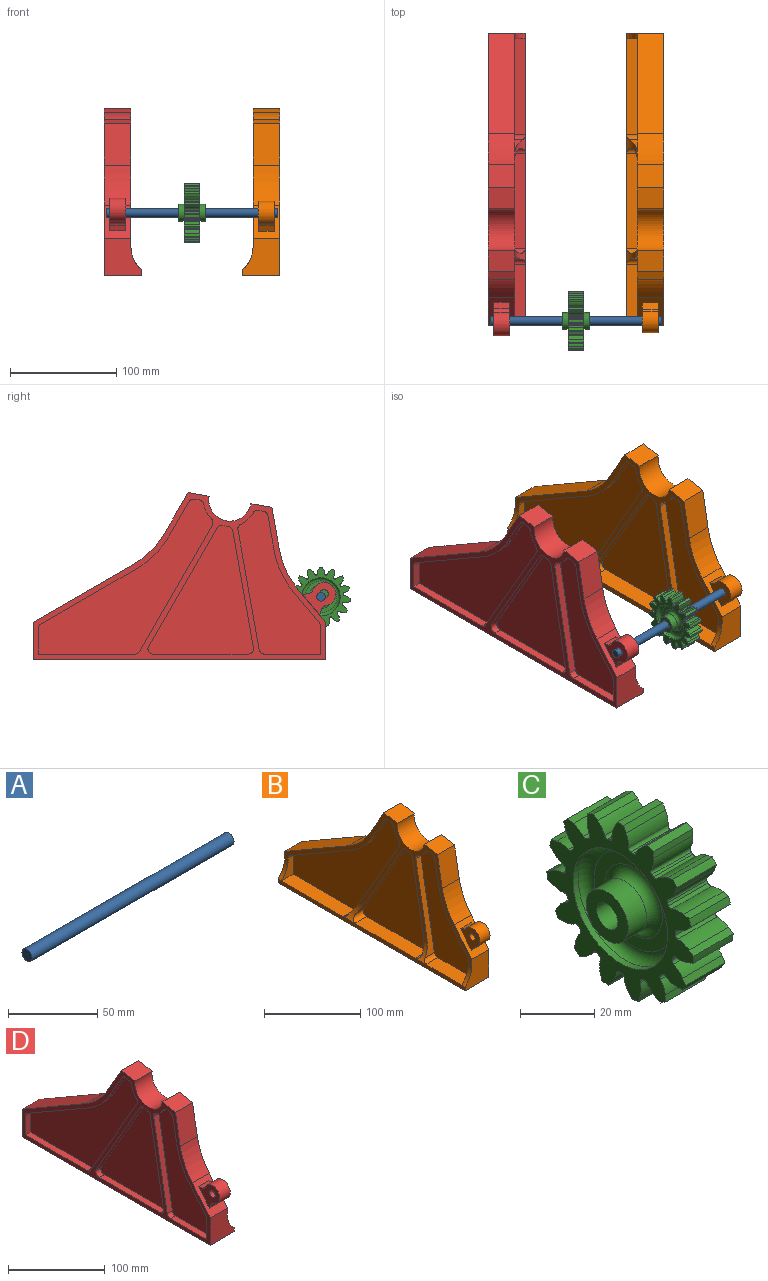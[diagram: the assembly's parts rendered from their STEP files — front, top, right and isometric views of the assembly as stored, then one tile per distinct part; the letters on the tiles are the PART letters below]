
ASSEMBLY  parts=4 mates=3
PART A: 3 faces, bbox 160x8x8 mm
  f0: cylinder r=4mm len=160mm, axis (-1,0,0), area 4021.2mm2, adj f1,f2
  f1: plane 8x8mm, normal (1,0,0), area 50.3mm2, adj f0
  f2: plane 8x8mm, normal (-1,0,0), area 50.3mm2, adj f0
PART B: 100 faces, bbox 35x281.6x156.9 mm
  f0: plane 31.19x26.17mm, normal (0,-0.77,0.64), area 642.9mm2, adj f29,f30,f36,f43,f92,f94,f96,f97
  f1: plane 89.24x17.5mm, normal (0,0,1), area 1561.7mm2, adj f7,f41,f64,f69
  f2: plane 90.51x17.5mm, normal (0,0,1), area 1583.9mm2, adj f15,f41,f54,f65
  f3: plane 90.51x7.5mm, normal (0,0,1), area 678.8mm2, adj f17,f22,f29,f73
  f4: cylinder r=25mm len=7.5mm, axis (1,0,0), area 36.1mm2, adj f8,f29,f71,f78
  f5: cylinder r=25mm len=7.5mm, axis (1,0,0), area 36.1mm2, adj f7,f30,f63,f70
  f6: plane 52.7x17.5mm, normal (0,0,1), area 922.2mm2, adj f14,f41,f53,f68
  f7: plane 121.09x99.24mm, normal (-1,0,0), area 7013.7mm2, adj f1,f5,f58,f61,f63,f64,f69,f70
  f8: plane 121.09x99.24mm, normal (1,0,0), area 7013.7mm2, adj f4,f9,f55,f60,f71,f72,f77,f78
  f9: plane 89.24x7.5mm, normal (0,0,1), area 669.3mm2, adj f8,f29,f72,f77
  f10: cylinder r=25mm len=11.41mm, axis (1,0,0), area 118mm2, adj f16,f29,f75,f81
  f11: cylinder r=25mm len=13.72mm, axis (1,0,0), area 118mm2, adj f17,f29,f74,f82
  f12: cylinder r=25mm len=11.41mm, axis (1,0,0), area 118mm2, adj f14,f30,f67,f88
  f13: cylinder r=25mm len=13.72mm, axis (1,0,0), area 118mm2, adj f15,f30,f66,f87
  f14: plane 135.24x77.57mm, normal (-1,0,0), area 5541.1mm2, adj f6,f12,f23,f27,f28,f50,f53,f57
  f15: plane 163.98x145.88mm, normal (-1,0,0), area 9003.2mm2, adj f2,f13,f24,f25,f26,f49,f54,f62
  f16: plane 135.24x77.57mm, normal (1,0,0), area 5541.1mm2, adj f10,f19,f20,f21,f45,f51,f52,f56
  f17: plane 163.98x146.41mm, normal (1,0,0), area 9005.4mm2, adj f3,f11,f18,f22,f46,f47,f48,f59
  f18: plane 8.09x7.5mm, normal (0,0.17,-0.98), area 61.6mm2, adj f17,f29,f48,f82
  f19: plane 7.5x4.64mm, normal (0,0.17,-0.98), area 35.4mm2, adj f16,f29,f81,f83
  f20: plane 26.36x7.5mm, normal (0,1,0), area 197.7mm2, adj f16,f21,f29,f79
  f21: plane 52.7x7.5mm, normal (0,0,1), area 395.2mm2, adj f16,f20,f29,f76
  f22: plane 24.23x7.5mm, normal (0,-1,0), area 181.7mm2, adj f3,f17,f29,f80
  f23: plane 28.4x23.83mm, normal (0,0.77,-0.64), area 278.1mm2, adj f14,f28,f30,f84
  f24: plane 89.24x51.52mm, normal (0,-0.5,-0.87), area 772.8mm2, adj f15,f25,f30,f85
  f25: cylinder r=85mm len=31.11mm, axis (1,0,0), area 333.8mm2, adj f15,f24,f26,f30
  f26: plane 32.19x18.59mm, normal (0,-0.87,-0.5), area 278.8mm2, adj f15,f25,f30,f86
  f27: plane 32.44x7.5mm, normal (0,0.98,-0.17), area 247mm2, adj f14,f28,f30,f89
  f28: cylinder r=85mm len=39.88mm, axis (1,0,0), area 333.8mm2, adj f14,f23,f27,f30
  f29: plane 275x156.95mm, normal (1,0,0), area 5097.7mm2, adj f0,f3,f4,f9,f10,f11,f18,f19
  f30: plane 275x129.59mm, normal (-1,0,0), area 3228.7mm2, adj f0,f5,f12,f13,f23,f24,f25,f26
  f31: cylinder r=30mm len=22.36mm, axis (0,-1,0), area 126.2mm2, adj f30,f36,f41,f53
  f32: plane 25x19.7mm, normal (0,-0.17,0.98), area 500mm2, adj f29,f30,f33,f40
  f33: cylinder r=20mm len=39.7mm, axis (-1,0,0), area 1570.8mm2, adj f29,f30,f32,f34
  f34: plane 25x19.7mm, normal (0,-0.17,0.98), area 500mm2, adj f29,f30,f33,f35
  f35: plane 39.33x25mm, normal (0,-0.98,0.17), area 998.5mm2, adj f29,f30,f34,f43
  f36: plane 35x35mm, normal (0,-1,0), area 993.7mm2, adj f0,f29,f30,f31,f37,f41
  f37: plane 275x35mm, normal (0,0,-1), area 9625mm2, adj f29,f36,f38,f41
  f38: plane 35x35mm, normal (0,1,0), area 993.7mm2, adj f29,f30,f37,f39,f41,f42
  f39: plane 94.24x54.41mm, normal (0,0.5,0.87), area 2720.5mm2, adj f29,f30,f38,f44
  f40: plane 38.26x25mm, normal (0,0.87,0.5), area 1104.3mm2, adj f29,f30,f32,f44
  f41: plane 275x5mm, normal (-1,0,0), area 1375mm2, adj f1,f2,f6,f31,f36,f37,f38,f42
  f42: cylinder r=30mm len=22.36mm, axis (0,-1,0), area 126.2mm2, adj f30,f38,f41,f54
  f43: cylinder r=80mm len=37.53mm, axis (1,0,0), area 1047.2mm2, adj f0,f29,f30,f35
  f44: cylinder r=80mm len=29.28mm, axis (1,0,0), area 1047.2mm2, adj f29,f30,f39,f40
  f45: plane 28.4x23.83mm, normal (0,0.77,-0.64), area 278.1mm2, adj f16,f29,f52,f79
  f46: plane 89.24x51.52mm, normal (0,-0.5,-0.87), area 772.8mm2, adj f17,f29,f47,f80
  f47: cylinder r=85mm len=31.11mm, axis (1,0,0), area 333.8mm2, adj f17,f29,f46,f48
  f48: plane 35.22x20.34mm, normal (0,-0.87,-0.5), area 305mm2, adj f17,f18,f29,f47
  f49: plane 7.5x4.64mm, normal (0,0.17,-0.98), area 35.4mm2, adj f15,f30,f86,f87
  f50: plane 7.5x4.64mm, normal (0,0.17,-0.98), area 35.4mm2, adj f14,f30,f88,f89
  f51: plane 32.44x7.5mm, normal (0,0.98,-0.17), area 247mm2, adj f16,f29,f52,f83
  f52: cylinder r=85mm len=39.88mm, axis (1,0,0), area 333.8mm2, adj f16,f29,f45,f51
  f53: plane 26.36x17.5mm, normal (0,1,0), area 266.4mm2, adj f6,f14,f30,f31,f84
  f54: plane 24.23x17.5mm, normal (0,-1,0), area 250.4mm2, adj f2,f15,f30,f42,f85
  f55: plane 110.09x19.41mm, normal (0,0.98,-0.17), area 838.4mm2, adj f8,f29,f77,f78
  f56: plane 112.7x19.87mm, normal (0,-0.98,0.17), area 858.3mm2, adj f16,f29,f75,f76
  f57: plane 112.7x19.87mm, normal (0,-0.98,0.17), area 894.6mm2, adj f14,f30,f67,f68,f91
  f58: plane 110.09x19.41mm, normal (0,0.98,-0.17), area 865mm2, adj f7,f30,f69,f70,f91
  f59: plane 118.59x68.47mm, normal (0,0.87,0.5), area 1027.1mm2, adj f17,f29,f73,f74
  f60: plane 111.09x64.14mm, normal (0,-0.87,-0.5), area 962.1mm2, adj f8,f29,f71,f72
  f61: plane 111.09x64.14mm, normal (0,-0.87,-0.5), area 984mm2, adj f7,f30,f63,f64,f90
  f62: plane 118.59x68.47mm, normal (0,0.87,0.5), area 1081.3mm2, adj f15,f30,f65,f66,f90
  f63: cylinder r=5mm len=7.5mm, axis (1,0,0), area 49.4mm2, adj f5,f7,f30,f61
  f64: cylinder r=5mm len=17.5mm, axis (-1,0,0), area 155.5mm2, adj f1,f7,f61,f90
  f65: cylinder r=5mm len=17.5mm, axis (-1,0,0), area 86.9mm2, adj f2,f15,f62,f90
  f66: cylinder r=5mm len=7.5mm, axis (1,0,0), area 49.4mm2, adj f13,f15,f30,f62
  f67: cylinder r=5mm len=7.5mm, axis (1,0,0), area 49.4mm2, adj f12,f14,f30,f57
  f68: cylinder r=5mm len=17.5mm, axis (1,0,0), area 112mm2, adj f6,f14,f57,f91
  f69: cylinder r=5mm len=17.5mm, axis (1,0,0), area 134.7mm2, adj f1,f7,f58,f91
  f70: cylinder r=5mm len=7.5mm, axis (1,0,0), area 49.4mm2, adj f5,f7,f30,f58
  f71: cylinder r=5mm len=7.5mm, axis (1,0,0), area 49.4mm2, adj f4,f8,f29,f60
  f72: cylinder r=5mm len=7.5mm, axis (-1,0,0), area 78.5mm2, adj f8,f9,f29,f60
  f73: cylinder r=5mm len=7.5mm, axis (-1,0,0), area 39.3mm2, adj f3,f17,f29,f59
  f74: cylinder r=5mm len=7.5mm, axis (1,0,0), area 49.4mm2, adj f11,f17,f29,f59
  f75: cylinder r=5mm len=7.5mm, axis (1,0,0), area 49.4mm2, adj f10,f16,f29,f56
  f76: cylinder r=5mm len=7.5mm, axis (1,0,0), area 52.4mm2, adj f16,f21,f29,f56
  f77: cylinder r=5mm len=7.5mm, axis (1,0,0), area 65.4mm2, adj f8,f9,f29,f55
  f78: cylinder r=5mm len=7.5mm, axis (1,0,0), area 49.4mm2, adj f4,f8,f29,f55
  f79: cylinder r=5mm len=7.5mm, axis (-1,0,0), area 26.2mm2, adj f16,f20,f29,f45
  f80: cylinder r=5mm len=7.5mm, axis (-1,0,0), area 39.3mm2, adj f17,f22,f29,f46
  f81: cylinder r=5mm len=7.5mm, axis (1,0,0), area 46.2mm2, adj f10,f16,f19,f29
  f82: cylinder r=5mm len=7.5mm, axis (1,0,0), area 46.2mm2, adj f11,f17,f18,f29
  f83: cylinder r=5mm len=7.5mm, axis (1,0,0), area 45.8mm2, adj f16,f19,f29,f51
  f84: cylinder r=5mm len=7.5mm, axis (-1,0,0), area 26.2mm2, adj f14,f23,f30,f53
  f85: cylinder r=5mm len=7.5mm, axis (-1,0,0), area 39.3mm2, adj f15,f24,f30,f54
  f86: cylinder r=5mm len=7.5mm, axis (1,0,0), area 45.8mm2, adj f15,f26,f30,f49
  f87: cylinder r=5mm len=7.5mm, axis (1,0,0), area 46.2mm2, adj f13,f15,f30,f49
  f88: cylinder r=5mm len=7.5mm, axis (1,0,0), area 46.2mm2, adj f12,f14,f30,f50
  f89: cylinder r=5mm len=7.5mm, axis (1,0,0), area 45.8mm2, adj f14,f27,f30,f50
  f90: cylinder r=30mm len=22.36mm, axis (0,1,0), area 171.3mm2, adj f30,f41,f61,f62,f64,f65
  f91: cylinder r=30mm len=22.36mm, axis (0,1,0), area 144.4mm2, adj f30,f41,f57,f58,f68,f69
  f92: plane 15x6.21mm, normal (0,0.41,0.91), area 102.3mm2, adj f0,f96,f97,f98
  f93: cylinder r=11mm len=20.94mm, axis (-1,0,0), area 602.7mm2, adj f96,f97,f98,f99
  f94: plane 15x5.63mm, normal (0,-0.83,-0.56), area 102.3mm2, adj f0,f96,f97,f99
  f95: cylinder r=4mm len=15mm, axis (-1,0,0), area 377mm2, adj f96,f97
  f96: plane 28.26x28.19mm, normal (1,0,0), area 407.4mm2, adj f0,f92,f93,f94,f95,f98,f99
  f97: plane 28.26x28.19mm, normal (-1,0,0), area 407.4mm2, adj f0,f92,f93,f94,f95,f98,f99
  f98: cylinder r=5mm len=15mm, axis (-1,0,0), area 39.6mm2, adj f92,f93,f96,f97
  f99: cylinder r=5mm len=15mm, axis (-1,0,0), area 39.6mm2, adj f93,f94,f96,f97
PART C: 135 faces, bbox 25x55.9x55.6 mm
  f0: cylinder r=18mm len=36mm, axis (-1,0,0), area 226.2mm2, adj f8,f134
  f1: cylinder r=21mm len=15mm, axis (-1,0,0), area 12.2mm2, adj f7,f8,f12,f19
  f2: cylinder r=18mm len=36mm, axis (-1,0,0), area 226.2mm2, adj f7,f133
  f3: cylinder r=21mm len=15mm, axis (-1,0,0), area 12.2mm2, adj f7,f8,f11,f123
  f4: plane 15x1.89mm, normal (0,0.88,0.47), area 32.3mm2, adj f5,f7,f8,f9
  f5: cylinder r=28mm len=15mm, axis (-1,0,0), area 36mm2, adj f4,f6,f7,f8
  f6: plane 15x1.89mm, normal (0,-0.88,0.47), area 32.3mm2, adj f5,f7,f8,f10
  f7: plane 55.89x55.61mm, normal (1,0,0), area 925.8mm2, adj f1,f2,f3,f4,f5,f6,f9,f10
  f8: plane 55.89x55.61mm, normal (-1,0,0), area 925.8mm2, adj f0,f1,f3,f4,f5,f6,f9,f10
  f9: cylinder r=8mm len=15mm, axis (1,0,0), area 68.4mm2, adj f4,f7,f8,f11
  f10: cylinder r=8mm len=15mm, axis (1,0,0), area 68.4mm2, adj f6,f7,f8,f12
  f11: cylinder r=1mm len=15mm, axis (1,0,0), area 21.8mm2, adj f3,f7,f8,f9
  f12: cylinder r=1mm len=15mm, axis (1,0,0), area 21.8mm2, adj f1,f7,f8,f10
  f13: cylinder r=21mm len=15mm, axis (-1,0,0), area 12.2mm2, adj f7,f8,f20,f27
  f14: plane 15x1.7mm, normal (0,0.61,0.79), area 32.3mm2, adj f7,f8,f15,f17
  f15: cylinder r=28mm len=15mm, axis (-1,0,0), area 36mm2, adj f7,f8,f14,f16
  f16: plane 15x2.15mm, normal (0,-1,0.08), area 32.3mm2, adj f7,f8,f15,f18
  f17: cylinder r=8mm len=15mm, axis (1,0,0), area 68.4mm2, adj f7,f8,f14,f19
  f18: cylinder r=8mm len=15mm, axis (1,0,0), area 68.4mm2, adj f7,f8,f16,f20
  f19: cylinder r=1mm len=15mm, axis (1,0,0), area 21.8mm2, adj f1,f7,f8,f17
  f20: cylinder r=1mm len=15mm, axis (1,0,0), area 21.8mm2, adj f7,f8,f13,f18
  f21: cylinder r=21mm len=15mm, axis (-1,0,0), area 12.2mm2, adj f7,f8,f28,f35
  f22: plane 15x2.09mm, normal (0,0.24,0.97), area 32.3mm2, adj f7,f8,f23,f25
  f23: cylinder r=28mm len=15mm, axis (-1,0,0), area 36mm2, adj f7,f8,f22,f24
  f24: plane 15x2.03mm, normal (0,-0.94,-0.34), area 32.3mm2, adj f7,f8,f23,f26
  f25: cylinder r=8mm len=15mm, axis (1,0,0), area 68.4mm2, adj f7,f8,f22,f27
  f26: cylinder r=8mm len=15mm, axis (1,0,0), area 68.4mm2, adj f7,f8,f24,f28
  f27: cylinder r=1mm len=15mm, axis (1,0,0), area 21.8mm2, adj f7,f8,f13,f25
  f28: cylinder r=1mm len=15mm, axis (1,0,0), area 21.8mm2, adj f7,f8,f21,f26
  f29: cylinder r=21mm len=15mm, axis (-1,0,0), area 12.2mm2, adj f7,f8,f36,f43
  f30: plane 15x2.12mm, normal (0,-0.18,0.98), area 32.3mm2, adj f7,f8,f31,f33
  f31: cylinder r=28mm len=15mm, axis (-1,0,0), area 36mm2, adj f7,f8,f30,f32
  f32: plane 15x1.56mm, normal (0,-0.72,-0.69), area 32.3mm2, adj f7,f8,f31,f34
  f33: cylinder r=8mm len=15mm, axis (1,0,0), area 68.4mm2, adj f7,f8,f30,f35
  f34: cylinder r=8mm len=15mm, axis (1,0,0), area 68.4mm2, adj f7,f8,f32,f36
  f35: cylinder r=1mm len=15mm, axis (1,0,0), area 21.8mm2, adj f7,f8,f21,f33
  f36: cylinder r=1mm len=15mm, axis (1,0,0), area 21.8mm2, adj f7,f8,f29,f34
  f37: cylinder r=21mm len=15mm, axis (-1,0,0), area 12.2mm2, adj f7,f8,f44,f51
  f38: plane 15x1.78mm, normal (0,-0.56,0.83), area 32.3mm2, adj f7,f8,f39,f41
  f39: cylinder r=28mm len=15mm, axis (-1,0,0), area 36mm2, adj f7,f8,f38,f40
  f40: plane 15x1.99mm, normal (0,-0.38,-0.92), area 32.3mm2, adj f7,f8,f39,f42
  f41: cylinder r=8mm len=15mm, axis (1,0,0), area 68.4mm2, adj f7,f8,f38,f43
  f42: cylinder r=8mm len=15mm, axis (1,0,0), area 68.4mm2, adj f7,f8,f40,f44
  f43: cylinder r=1mm len=15mm, axis (1,0,0), area 21.8mm2, adj f7,f8,f29,f41
  f44: cylinder r=1mm len=15mm, axis (1,0,0), area 21.8mm2, adj f7,f8,f37,f42
  f45: cylinder r=21mm len=15mm, axis (-1,0,0), area 12.2mm2, adj f7,f8,f52,f59
  f46: plane 15x1.83mm, normal (0,-0.85,0.52), area 32.3mm2, adj f7,f8,f47,f49
  f47: cylinder r=28mm len=15mm, axis (-1,0,0), area 36mm2, adj f7,f8,f46,f48
  f48: plane 15x2.15mm, normal (0,0.03,-1), area 32.3mm2, adj f7,f8,f47,f50
  f49: cylinder r=8mm len=15mm, axis (1,0,0), area 68.4mm2, adj f7,f8,f46,f51
  f50: cylinder r=8mm len=15mm, axis (1,0,0), area 68.4mm2, adj f7,f8,f48,f52
  f51: cylinder r=1mm len=15mm, axis (1,0,0), area 21.8mm2, adj f7,f8,f37,f49
  f52: cylinder r=1mm len=15mm, axis (1,0,0), area 21.8mm2, adj f7,f8,f45,f50
  f53: cylinder r=21mm len=15mm, axis (-1,0,0), area 12.2mm2, adj f7,f8,f60,f67
  f54: plane 15x2.13mm, normal (0,-0.99,0.13), area 32.3mm2, adj f7,f8,f55,f57
  f55: cylinder r=28mm len=15mm, axis (-1,0,0), area 36mm2, adj f7,f8,f54,f56
  f56: plane 15x1.94mm, normal (0,0.43,-0.9), area 32.3mm2, adj f7,f8,f55,f58
  f57: cylinder r=8mm len=15mm, axis (1,0,0), area 68.4mm2, adj f7,f8,f54,f59
  f58: cylinder r=8mm len=15mm, axis (1,0,0), area 68.4mm2, adj f7,f8,f56,f60
  f59: cylinder r=1mm len=15mm, axis (1,0,0), area 21.8mm2, adj f7,f8,f45,f57
  f60: cylinder r=1mm len=15mm, axis (1,0,0), area 21.8mm2, adj f7,f8,f53,f58
  f61: cylinder r=21mm len=15mm, axis (-1,0,0), area 12.2mm2, adj f7,f8,f68,f75
  f62: plane 15x2.06mm, normal (0,-0.96,-0.28), area 32.3mm2, adj f7,f8,f63,f65
  f63: cylinder r=28mm len=15mm, axis (-1,0,0), area 36mm2, adj f7,f8,f62,f64
  f64: plane 15x1.64mm, normal (0,0.76,-0.65), area 32.3mm2, adj f7,f8,f63,f66
  f65: cylinder r=8mm len=15mm, axis (1,0,0), area 68.4mm2, adj f7,f8,f62,f67
  f66: cylinder r=8mm len=15mm, axis (1,0,0), area 68.4mm2, adj f7,f8,f64,f68
  f67: cylinder r=1mm len=15mm, axis (1,0,0), area 21.8mm2, adj f7,f8,f53,f65
  f68: cylinder r=1mm len=15mm, axis (1,0,0), area 21.8mm2, adj f7,f8,f61,f66
  f69: cylinder r=21mm len=15mm, axis (-1,0,0), area 12.2mm2, adj f7,f8,f76,f83
  f70: plane 15x1.64mm, normal (0,-0.76,-0.65), area 32.3mm2, adj f7,f8,f71,f73
  f71: cylinder r=28mm len=15mm, axis (-1,0,0), area 36mm2, adj f7,f8,f70,f72
  f72: plane 15x2.06mm, normal (0,0.96,-0.28), area 32.3mm2, adj f7,f8,f71,f74
  f73: cylinder r=8mm len=15mm, axis (1,0,0), area 68.4mm2, adj f7,f8,f70,f75
  f74: cylinder r=8mm len=15mm, axis (1,0,0), area 68.4mm2, adj f7,f8,f72,f76
  f75: cylinder r=1mm len=15mm, axis (1,0,0), area 21.8mm2, adj f7,f8,f61,f73
  f76: cylinder r=1mm len=15mm, axis (1,0,0), area 21.8mm2, adj f7,f8,f69,f74
  f77: cylinder r=21mm len=15mm, axis (-1,0,0), area 12.2mm2, adj f7,f8,f84,f91
  f78: plane 15x1.94mm, normal (0,-0.43,-0.9), area 32.3mm2, adj f7,f8,f79,f81
  f79: cylinder r=28mm len=15mm, axis (-1,0,0), area 36mm2, adj f7,f8,f78,f80
  f80: plane 15x2.13mm, normal (0,0.99,0.13), area 32.3mm2, adj f7,f8,f79,f82
  f81: cylinder r=8mm len=15mm, axis (1,0,0), area 68.4mm2, adj f7,f8,f78,f83
  f82: cylinder r=8mm len=15mm, axis (1,0,0), area 68.4mm2, adj f7,f8,f80,f84
  f83: cylinder r=1mm len=15mm, axis (1,0,0), area 21.8mm2, adj f7,f8,f69,f81
  f84: cylinder r=1mm len=15mm, axis (1,0,0), area 21.8mm2, adj f7,f8,f77,f82
  f85: cylinder r=21mm len=15mm, axis (-1,0,0), area 12.2mm2, adj f7,f8,f92,f99
  f86: plane 15x2.15mm, normal (0,-0.03,-1), area 32.3mm2, adj f7,f8,f87,f89
  f87: cylinder r=28mm len=15mm, axis (-1,0,0), area 36mm2, adj f7,f8,f86,f88
  f88: plane 15x1.83mm, normal (0,0.85,0.52), area 32.3mm2, adj f7,f8,f87,f90
  f89: cylinder r=8mm len=15mm, axis (1,0,0), area 68.4mm2, adj f7,f8,f86,f91
  f90: cylinder r=8mm len=15mm, axis (1,0,0), area 68.4mm2, adj f7,f8,f88,f92
  f91: cylinder r=1mm len=15mm, axis (1,0,0), area 21.8mm2, adj f7,f8,f77,f89
  f92: cylinder r=1mm len=15mm, axis (1,0,0), area 21.8mm2, adj f7,f8,f85,f90
  f93: cylinder r=21mm len=15mm, axis (-1,0,0), area 12.2mm2, adj f7,f8,f100,f107
  f94: plane 15x1.99mm, normal (0,0.38,-0.92), area 32.3mm2, adj f7,f8,f95,f97
  f95: cylinder r=28mm len=15mm, axis (-1,0,0), area 36mm2, adj f7,f8,f94,f96
  f96: plane 15x1.78mm, normal (0,0.56,0.83), area 32.3mm2, adj f7,f8,f95,f98
  f97: cylinder r=8mm len=15mm, axis (1,0,0), area 68.4mm2, adj f7,f8,f94,f99
  f98: cylinder r=8mm len=15mm, axis (1,0,0), area 68.4mm2, adj f7,f8,f96,f100
  f99: cylinder r=1mm len=15mm, axis (1,0,0), area 21.8mm2, adj f7,f8,f85,f97
  f100: cylinder r=1mm len=15mm, axis (1,0,0), area 21.8mm2, adj f7,f8,f93,f98
  f101: cylinder r=21mm len=15mm, axis (-1,0,0), area 12.2mm2, adj f7,f8,f108,f115
  f102: plane 15x1.56mm, normal (0,0.72,-0.69), area 32.3mm2, adj f7,f8,f103,f105
  f103: cylinder r=28mm len=15mm, axis (-1,0,0), area 36mm2, adj f7,f8,f102,f104
  f104: plane 15x2.12mm, normal (0,0.18,0.98), area 32.3mm2, adj f7,f8,f103,f106
  f105: cylinder r=8mm len=15mm, axis (1,0,0), area 68.4mm2, adj f7,f8,f102,f107
  f106: cylinder r=8mm len=15mm, axis (1,0,0), area 68.4mm2, adj f7,f8,f104,f108
  f107: cylinder r=1mm len=15mm, axis (1,0,0), area 21.8mm2, adj f7,f8,f93,f105
  f108: cylinder r=1mm len=15mm, axis (1,0,0), area 21.8mm2, adj f7,f8,f101,f106
  f109: cylinder r=21mm len=15mm, axis (-1,0,0), area 12.2mm2, adj f7,f8,f116,f122
  f110: plane 15x2.03mm, normal (0,0.94,-0.34), area 32.3mm2, adj f7,f8,f111,f113
  f111: cylinder r=28mm len=15mm, axis (-1,0,0), area 36mm2, adj f7,f8,f110,f112
  f112: plane 15x2.09mm, normal (0,-0.24,0.97), area 32.3mm2, adj f7,f8,f111,f114
  f113: cylinder r=8mm len=15mm, axis (1,0,0), area 68.4mm2, adj f7,f8,f110,f115
  f114: cylinder r=8mm len=15mm, axis (1,0,0), area 68.4mm2, adj f7,f8,f112,f116
  f115: cylinder r=1mm len=15mm, axis (1,0,0), area 21.8mm2, adj f7,f8,f101,f113
  f116: cylinder r=1mm len=15mm, axis (1,0,0), area 21.8mm2, adj f7,f8,f109,f114
  f117: plane 15x2.15mm, normal (0,1,0.08), area 32.3mm2, adj f7,f8,f118,f120
  f118: cylinder r=28mm len=15mm, axis (-1,0,0), area 36mm2, adj f7,f8,f117,f119
  f119: plane 15x1.7mm, normal (0,-0.61,0.79), area 32.3mm2, adj f7,f8,f118,f121
  f120: cylinder r=8mm len=15mm, axis (1,0,0), area 68.4mm2, adj f7,f8,f117,f122
  f121: cylinder r=8mm len=15mm, axis (1,0,0), area 68.4mm2, adj f7,f8,f119,f123
  f122: cylinder r=1mm len=15mm, axis (1,0,0), area 21.8mm2, adj f7,f8,f109,f120
  f123: cylinder r=1mm len=15mm, axis (1,0,0), area 21.8mm2, adj f3,f7,f8,f121
  f124: plane 30x30mm, normal (1,0,0), area 326.7mm2, adj f131,f133
  f125: plane 30x30mm, normal (-1,0,0), area 326.7mm2, adj f132,f134
  f126: plane 16x16mm, normal (-1,0,0), area 150.8mm2, adj f127,f128
  f127: cylinder r=8mm len=16mm, axis (-1,0,0), area 351.9mm2, adj f126,f132
  f128: cylinder r=4mm len=25mm, axis (-1,0,0), area 628.3mm2, adj f126,f130
  f129: cylinder r=8mm len=16mm, axis (-1,0,0), area 351.9mm2, adj f130,f131
  f130: plane 16x16mm, normal (1,0,0), area 150.8mm2, adj f128,f129
  f131: torus R=11mm, axis (1,0,0), area 269.1mm2, adj f124,f129
  f132: torus R=11mm, axis (1,0,0), area 269.1mm2, adj f125,f127
  f133: torus R=15mm, axis (1,0,0), area 500.7mm2, adj f2,f124
  f134: torus R=15mm, axis (1,0,0), area 500.7mm2, adj f0,f125
PART D: 100 faces, bbox 35x284.4x156.9 mm
  f0: plane 31.19x26.17mm, normal (0,-0.77,0.64), area 642.9mm2, adj f28,f29,f35,f42,f92,f94,f96,f97
  f1: plane 89.24x17.5mm, normal (0,0,1), area 1561.7mm2, adj f8,f40,f72,f77
  f2: plane 90.51x17.5mm, normal (0,0,1), area 1583.9mm2, adj f17,f40,f54,f73
  f3: plane 52.7x17.5mm, normal (0,0,1), area 922.2mm2, adj f16,f20,f40,f76
  f4: cylinder r=25mm len=7.5mm, axis (1,0,0), area 36.1mm2, adj f8,f28,f71,f78
  f5: plane 90.51x7.5mm, normal (0,0,1), area 678.8mm2, adj f15,f21,f29,f65
  f6: cylinder r=25mm len=7.5mm, axis (1,0,0), area 36.1mm2, adj f7,f29,f63,f70
  f7: plane 121.09x99.24mm, normal (-1,0,0), area 7013.7mm2, adj f6,f11,f58,f61,f63,f64,f69,f70
  f8: plane 121.09x99.24mm, normal (1,0,0), area 7013.7mm2, adj f1,f4,f55,f60,f71,f72,f77,f78
  f9: cylinder r=25mm len=11.41mm, axis (1,0,0), area 118mm2, adj f16,f28,f75,f82
  f10: cylinder r=25mm len=13.72mm, axis (1,0,0), area 118mm2, adj f17,f28,f74,f81
  f11: plane 89.24x7.5mm, normal (0,0,1), area 669.3mm2, adj f7,f29,f64,f69
  f12: cylinder r=25mm len=11.41mm, axis (1,0,0), area 118mm2, adj f14,f29,f67,f88
  f13: cylinder r=25mm len=13.72mm, axis (1,0,0), area 118mm2, adj f15,f29,f66,f87
  f14: plane 135.24x77.57mm, normal (-1,0,0), area 5541.1mm2, adj f12,f22,f26,f27,f45,f50,f53,f57
  f15: plane 163.98x145.88mm, normal (-1,0,0), area 9003.2mm2, adj f5,f13,f21,f23,f24,f25,f49,f62
  f16: plane 135.24x77.57mm, normal (1,0,0), area 5541.1mm2, adj f3,f9,f19,f20,f44,f51,f52,f56
  f17: plane 163.98x146.41mm, normal (1,0,0), area 9005.4mm2, adj f2,f10,f18,f46,f47,f48,f54,f59
  f18: plane 8.09x7.5mm, normal (0,0.17,-0.98), area 61.6mm2, adj f17,f28,f48,f81
  f19: plane 7.5x4.64mm, normal (0,0.17,-0.98), area 35.4mm2, adj f16,f28,f82,f83
  f20: plane 26.36x17.5mm, normal (0,1,0), area 266.4mm2, adj f3,f16,f28,f30,f79
  f21: plane 24.23x7.5mm, normal (0,-1,0), area 181.7mm2, adj f5,f15,f29,f85
  f22: plane 28.4x23.83mm, normal (0,0.77,-0.64), area 278.1mm2, adj f14,f27,f29,f84
  f23: plane 89.24x51.52mm, normal (0,-0.5,-0.87), area 772.8mm2, adj f15,f24,f29,f85
  f24: cylinder r=85mm len=31.11mm, axis (1,0,0), area 333.8mm2, adj f15,f23,f25,f29
  f25: plane 32.19x18.59mm, normal (0,-0.87,-0.5), area 278.8mm2, adj f15,f24,f29,f86
  f26: plane 32.44x7.5mm, normal (0,0.98,-0.17), area 247mm2, adj f14,f27,f29,f89
  f27: cylinder r=85mm len=39.88mm, axis (1,0,0), area 333.8mm2, adj f14,f22,f26,f29
  f28: plane 275x129.59mm, normal (1,0,0), area 3226.5mm2, adj f0,f4,f9,f10,f18,f19,f20,f30
  f29: plane 275x156.95mm, normal (-1,0,0), area 5099.9mm2, adj f0,f5,f6,f11,f12,f13,f21,f22
  f30: cylinder r=30mm len=22.36mm, axis (0,1,0), area 126.2mm2, adj f20,f28,f35,f40
  f31: plane 25x19.7mm, normal (0,-0.17,0.98), area 500mm2, adj f28,f29,f32,f39
  f32: cylinder r=20mm len=39.7mm, axis (-1,0,0), area 1570.8mm2, adj f28,f29,f31,f33
  f33: plane 25x19.7mm, normal (0,-0.17,0.98), area 500mm2, adj f28,f29,f32,f34
  f34: plane 39.33x25mm, normal (0,-0.98,0.17), area 998.5mm2, adj f28,f29,f33,f42
  f35: plane 35x35mm, normal (0,-1,0), area 993.7mm2, adj f0,f28,f29,f30,f36,f40
  f36: plane 275x35mm, normal (0,0,-1), area 9625mm2, adj f29,f35,f37,f40
  f37: plane 35x35mm, normal (0,1,0), area 993.7mm2, adj f28,f29,f36,f38,f40,f41
  f38: plane 94.24x54.41mm, normal (0,0.5,0.87), area 2720.5mm2, adj f28,f29,f37,f43
  f39: plane 38.26x25mm, normal (0,0.87,0.5), area 1104.3mm2, adj f28,f29,f31,f43
  f40: plane 275x5mm, normal (1,0,0), area 1375mm2, adj f1,f2,f3,f30,f35,f36,f37,f41
  f41: cylinder r=30mm len=22.36mm, axis (0,1,0), area 126.2mm2, adj f28,f37,f40,f54
  f42: cylinder r=80mm len=37.53mm, axis (1,0,0), area 1047.2mm2, adj f0,f28,f29,f34
  f43: cylinder r=80mm len=29.28mm, axis (1,0,0), area 1047.2mm2, adj f28,f29,f38,f39
  f44: plane 28.4x23.83mm, normal (0,0.77,-0.64), area 278.1mm2, adj f16,f28,f52,f79
  f45: plane 52.7x7.5mm, normal (0,0,1), area 395.2mm2, adj f14,f29,f53,f68
  f46: plane 89.24x51.52mm, normal (0,-0.5,-0.87), area 772.8mm2, adj f17,f28,f47,f80
  f47: cylinder r=85mm len=31.11mm, axis (1,0,0), area 333.8mm2, adj f17,f28,f46,f48
  f48: plane 35.22x20.34mm, normal (0,-0.87,-0.5), area 305mm2, adj f17,f18,f28,f47
  f49: plane 7.5x4.64mm, normal (0,0.17,-0.98), area 35.4mm2, adj f15,f29,f86,f87
  f50: plane 7.5x4.64mm, normal (0,0.17,-0.98), area 35.4mm2, adj f14,f29,f88,f89
  f51: plane 32.44x7.5mm, normal (0,0.98,-0.17), area 247mm2, adj f16,f28,f52,f83
  f52: cylinder r=85mm len=39.88mm, axis (1,0,0), area 333.8mm2, adj f16,f28,f44,f51
  f53: plane 26.36x7.5mm, normal (0,1,0), area 197.7mm2, adj f14,f29,f45,f84
  f54: plane 24.23x17.5mm, normal (0,-1,0), area 250.4mm2, adj f2,f17,f28,f41,f80
  f55: plane 110.09x19.41mm, normal (0,0.98,-0.17), area 865mm2, adj f8,f28,f77,f78,f91
  f56: plane 112.7x19.87mm, normal (0,-0.98,0.17), area 894.6mm2, adj f16,f28,f75,f76,f91
  f57: plane 112.7x19.87mm, normal (0,-0.98,0.17), area 858.3mm2, adj f14,f29,f67,f68
  f58: plane 110.09x19.41mm, normal (0,0.98,-0.17), area 838.4mm2, adj f7,f29,f69,f70
  f59: plane 118.59x68.47mm, normal (0,0.87,0.5), area 1081.3mm2, adj f17,f28,f73,f74,f90
  f60: plane 111.09x64.14mm, normal (0,-0.87,-0.5), area 984mm2, adj f8,f28,f71,f72,f90
  f61: plane 111.09x64.14mm, normal (0,-0.87,-0.5), area 962.1mm2, adj f7,f29,f63,f64
  f62: plane 118.59x68.47mm, normal (0,0.87,0.5), area 1027.1mm2, adj f15,f29,f65,f66
  f63: cylinder r=5mm len=7.5mm, axis (1,0,0), area 49.4mm2, adj f6,f7,f29,f61
  f64: cylinder r=5mm len=7.5mm, axis (-1,0,0), area 78.5mm2, adj f7,f11,f29,f61
  f65: cylinder r=5mm len=7.5mm, axis (-1,0,0), area 39.3mm2, adj f5,f15,f29,f62
  f66: cylinder r=5mm len=7.5mm, axis (1,0,0), area 49.4mm2, adj f13,f15,f29,f62
  f67: cylinder r=5mm len=7.5mm, axis (1,0,0), area 49.4mm2, adj f12,f14,f29,f57
  f68: cylinder r=5mm len=7.5mm, axis (1,0,0), area 52.4mm2, adj f14,f29,f45,f57
  f69: cylinder r=5mm len=7.5mm, axis (1,0,0), area 65.4mm2, adj f7,f11,f29,f58
  f70: cylinder r=5mm len=7.5mm, axis (1,0,0), area 49.4mm2, adj f6,f7,f29,f58
  f71: cylinder r=5mm len=7.5mm, axis (1,0,0), area 49.4mm2, adj f4,f8,f28,f60
  f72: cylinder r=5mm len=17.5mm, axis (-1,0,0), area 155.5mm2, adj f1,f8,f60,f90
  f73: cylinder r=5mm len=17.5mm, axis (-1,0,0), area 86.9mm2, adj f2,f17,f59,f90
  f74: cylinder r=5mm len=7.5mm, axis (1,0,0), area 49.4mm2, adj f10,f17,f28,f59
  f75: cylinder r=5mm len=7.5mm, axis (1,0,0), area 49.4mm2, adj f9,f16,f28,f56
  f76: cylinder r=5mm len=17.5mm, axis (1,0,0), area 112mm2, adj f3,f16,f56,f91
  f77: cylinder r=5mm len=17.5mm, axis (1,0,0), area 134.7mm2, adj f1,f8,f55,f91
  f78: cylinder r=5mm len=7.5mm, axis (1,0,0), area 49.4mm2, adj f4,f8,f28,f55
  f79: cylinder r=5mm len=7.5mm, axis (-1,0,0), area 26.2mm2, adj f16,f20,f28,f44
  f80: cylinder r=5mm len=7.5mm, axis (-1,0,0), area 39.3mm2, adj f17,f28,f46,f54
  f81: cylinder r=5mm len=7.5mm, axis (1,0,0), area 46.2mm2, adj f10,f17,f18,f28
  f82: cylinder r=5mm len=7.5mm, axis (1,0,0), area 46.2mm2, adj f9,f16,f19,f28
  f83: cylinder r=5mm len=7.5mm, axis (1,0,0), area 45.8mm2, adj f16,f19,f28,f51
  f84: cylinder r=5mm len=7.5mm, axis (-1,0,0), area 26.2mm2, adj f14,f22,f29,f53
  f85: cylinder r=5mm len=7.5mm, axis (-1,0,0), area 39.3mm2, adj f15,f21,f23,f29
  f86: cylinder r=5mm len=7.5mm, axis (1,0,0), area 45.8mm2, adj f15,f25,f29,f49
  f87: cylinder r=5mm len=7.5mm, axis (1,0,0), area 46.2mm2, adj f13,f15,f29,f49
  f88: cylinder r=5mm len=7.5mm, axis (1,0,0), area 46.2mm2, adj f12,f14,f29,f50
  f89: cylinder r=5mm len=7.5mm, axis (1,0,0), area 45.8mm2, adj f14,f26,f29,f50
  f90: cylinder r=30mm len=22.36mm, axis (0,-1,0), area 171.3mm2, adj f28,f40,f59,f60,f72,f73
  f91: cylinder r=30mm len=22.36mm, axis (0,-1,0), area 144.4mm2, adj f28,f40,f55,f56,f76,f77
  f92: plane 15x5.85mm, normal (0,0.16,0.99), area 88.9mm2, adj f0,f96,f97,f98
  f93: cylinder r=11mm len=21.86mm, axis (-1,0,0), area 696.3mm2, adj f96,f97,f98,f99
  f94: plane 15x5.6mm, normal (0,-0.95,-0.32), area 88.9mm2, adj f0,f96,f97,f99
  f95: cylinder r=4mm len=15mm, axis (-1,0,0), area 377mm2, adj f96,f97
  f96: plane 31.19x30.78mm, normal (1,0,0), area 462mm2, adj f0,f92,f93,f94,f95,f98,f99
  f97: plane 31.19x30.78mm, normal (-1,0,0), area 462mm2, adj f0,f92,f93,f94,f95,f98,f99
  f98: cylinder r=5mm len=15mm, axis (-1,0,0), area 81.1mm2, adj f92,f93,f96,f97
  f99: cylinder r=5mm len=15mm, axis (-1,0,0), area 81.1mm2, adj f93,f94,f96,f97
PLACE A t=(14.09,-99.74,-50.15)mm
PLACE B t=(84.09,-14.17,40.97)mm
PLACE C t=(14.09,-99.74,-50.15)mm
PLACE D t=(-55.91,-14.17,40.97)mm
MATE fastened D.f32 <-> B.f33  axis (1,0,0) through (-43.41,-14.17,40.97)mm
MATE fastened C.f128 <-> A.f0  axis (-1,0,0) through (14.09,-99.74,-50.15)mm
MATE revolute A.f0 <-> B.f93  axis (-1,0,0) through (14.09,-99.74,-50.15)mm
